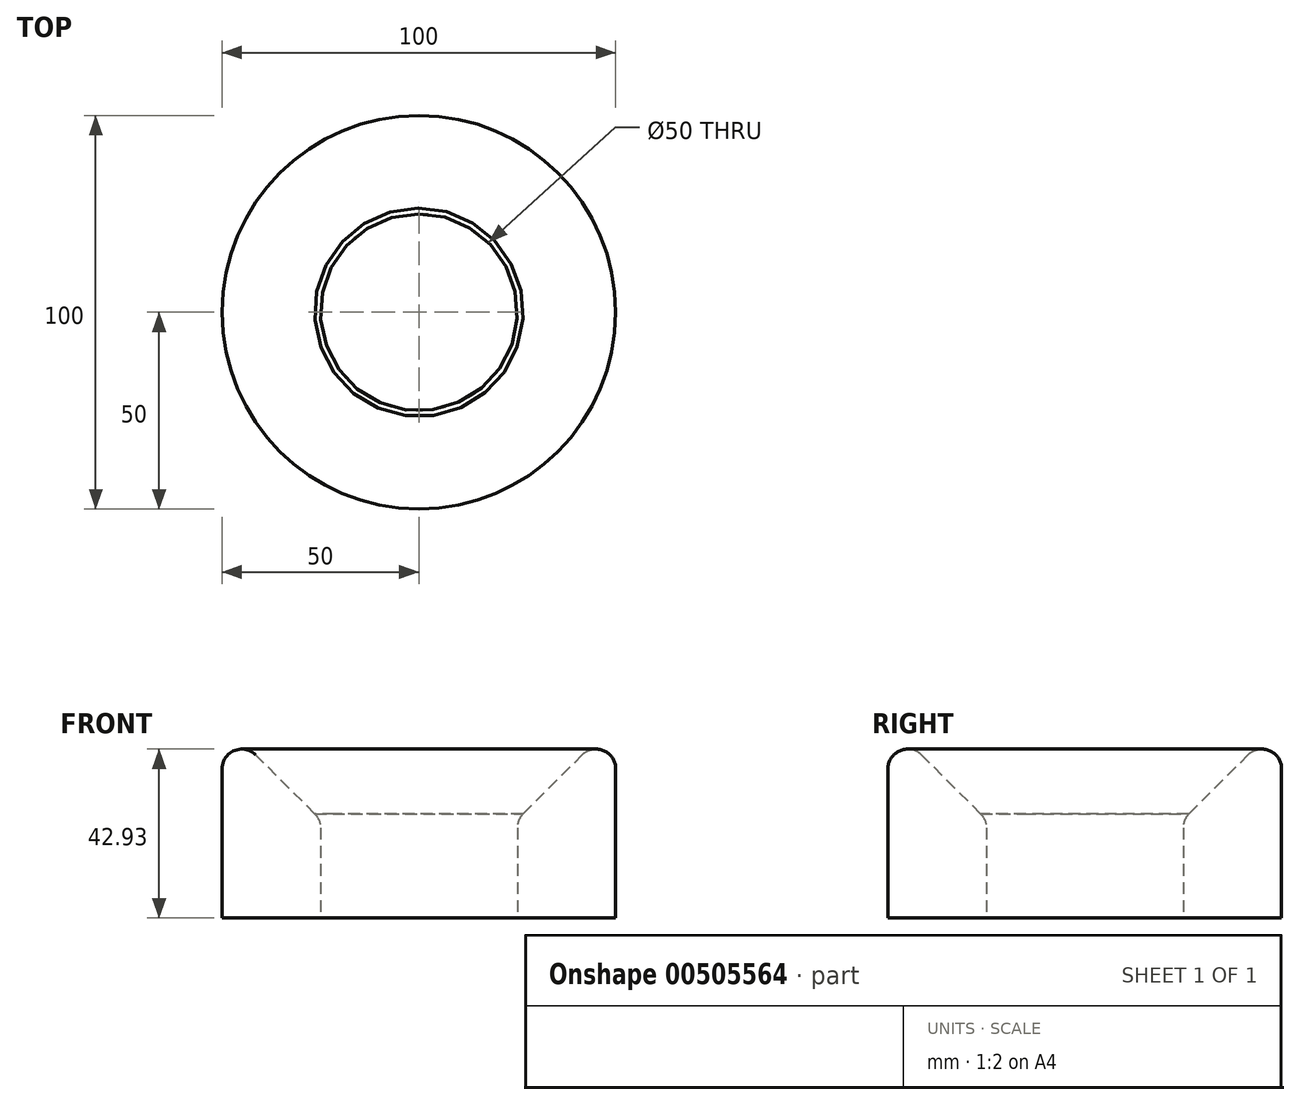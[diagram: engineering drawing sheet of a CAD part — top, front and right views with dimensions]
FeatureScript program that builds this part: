
annotation { "Feature Type Name" : "Feature", "Feature Type Description" : "" }
export const myFeature = defineFeature(function(context is Context, id is Id, definition is map)
    precondition{}
    {
        {
            var Q0;
            Q0=qCreatedBy(makeId("Front.planeOp"),FACE);
            var sketch = newSketch(context, id + "F0", { "sketchPlane" : qUnion([Q0])});
            skLineSegment(sketch, "E0", {"start": v(-50, 0) * mm, "end": v(-50, 50) * mm});
            skLineSegment(sketch, "E1", {"start": v(-50, 50) * mm, "end": v(0, 0) * mm});
            skLineSegment(sketch, "E2", {"start": v(0, 0) * mm, "end": v(0, 0) * mm});
            skLineSegment(sketch, "E3", {"start": v(-50, 0) * mm, "end": v(0, 0) * mm});
            skSolve(sketch);
        }
        {
            var Q0;
            Q0=qCreatedBy(makeId("Top.planeOp"),FACE);
            var sketch = newSketch(context, id + "F1", { "sketchPlane" : qUnion([Q0])});
            skCircle(sketch, "E4", {"center": v(0, 0) * mm, "radius": 25 * mm});
            skSolve(sketch);
        }
        {
            var Q0;
            Q0=makeQuery(id+"F0.imprint","IMPRINT",FACE,{"disambiguationData":[TD([[makeQuery(id+"F0.imprint","IMPRINT",EDGE,{"derivedFrom":sQuery(id+"F0.wireOp",EDGE,"E0")}),-1.0]])]});
            var Q1;
            Q1=sQuery(id+"F0.wireOp",EDGE,"E2");
            revolve(context, id + "F2", {"entities" : qUnion([Q0]), "axis" : qUnion([Q1]), "revolveType" : RevolveType.FULL});
        }
        {
            var Q0;
            Q0=makeQuery(id+"F1.imprint","IMPRINT",FACE,{"disambiguationData":[TD([[makeQuery(id+"F1.imprint","IMPRINT",EDGE,{"derivedFrom":sQuery(id+"F1.wireOp",EDGE,"E4")}),1.0]])]});
            extrude(context, id + "F3", {"entities" : qUnion([Q0]), "operationType" : NewBodyOperationType.REMOVE, "depth" : 48.2 * mm});
        }
        {
            var Q0;
            Q0=makeQuery(id+"F2.opRevolve","SWEPT_FACE",FACE,{"disambiguationData":[OSD([sQuery(id+"F0.wireOp",EDGE,"E1")])]});
            fillet(context, id + "F4", {"entities" : qUnion([Q0]), "radius" : 5 * mm, "tangentPropagation" : true, "allowEdgeOverflow" : false});
        }
    });
